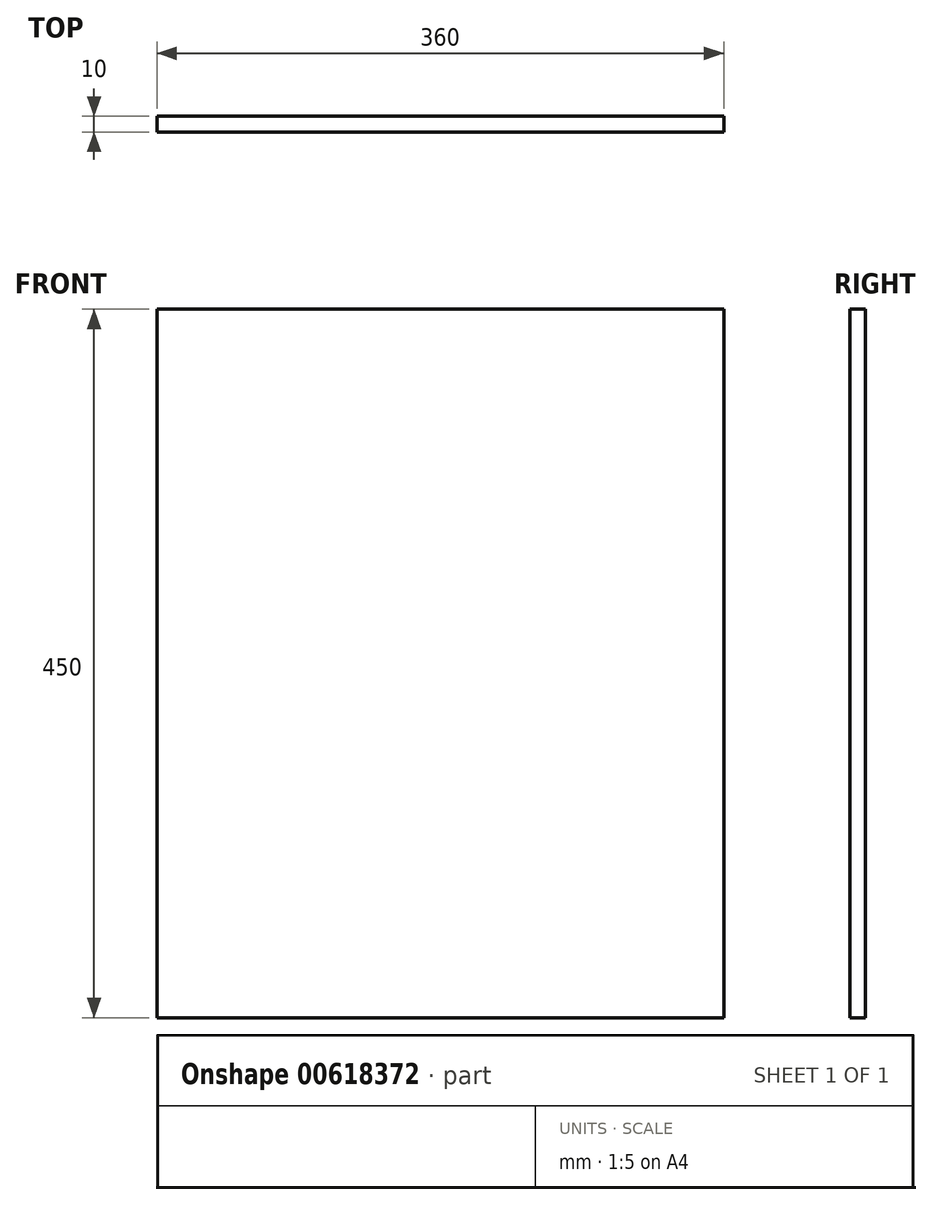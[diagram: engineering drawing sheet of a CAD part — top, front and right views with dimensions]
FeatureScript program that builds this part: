
annotation { "Feature Type Name" : "Feature", "Feature Type Description" : "" }
export const myFeature = defineFeature(function(context is Context, id is Id, definition is map)
    precondition{}
    {
        {
            var Q0;
            Q0=qCreatedBy(makeId("Front.planeOp"),FACE);
            var sketch = newSketch(context, id + "F0", { "sketchPlane" : qUnion([Q0])});
            skLineSegment(sketch, "E0.bottom", {"start": v(180, -225) * mm, "end": v(-180, -225) * mm});
            skLineSegment(sketch, "E0.top", {"start": v(180, 225) * mm, "end": v(-180, 225) * mm});
            skLineSegment(sketch, "E0.left", {"start": v(180, -225) * mm, "end": v(180, 225) * mm});
            skLineSegment(sketch, "E0.right", {"start": v(-180, -225) * mm, "end": v(-180, 225) * mm});
            skPoint(sketch, "E0.middle", {"position": v(0, 0) * mm});
            skSolve(sketch);
        }
        {
            var Q0;
            Q0=makeQuery(id+"F0.imprint","IMPRINT",FACE,{"disambiguationData":[TD([[makeQuery(id+"F0.imprint","IMPRINT",EDGE,{"derivedFrom":sQuery(id+"F0.wireOp",EDGE,"E0.bottom")}),-1.0]])]});
            extrude(context, id + "F1", {"entities" : qUnion([Q0]), "depth" : 5 * mm, "offsetDistance" : 25 * mm, "hasSecondDirection" : true, "secondDirectionOppositeDirection" : true, "secondDirectionDepth" : 5 * mm});
        }
    });
